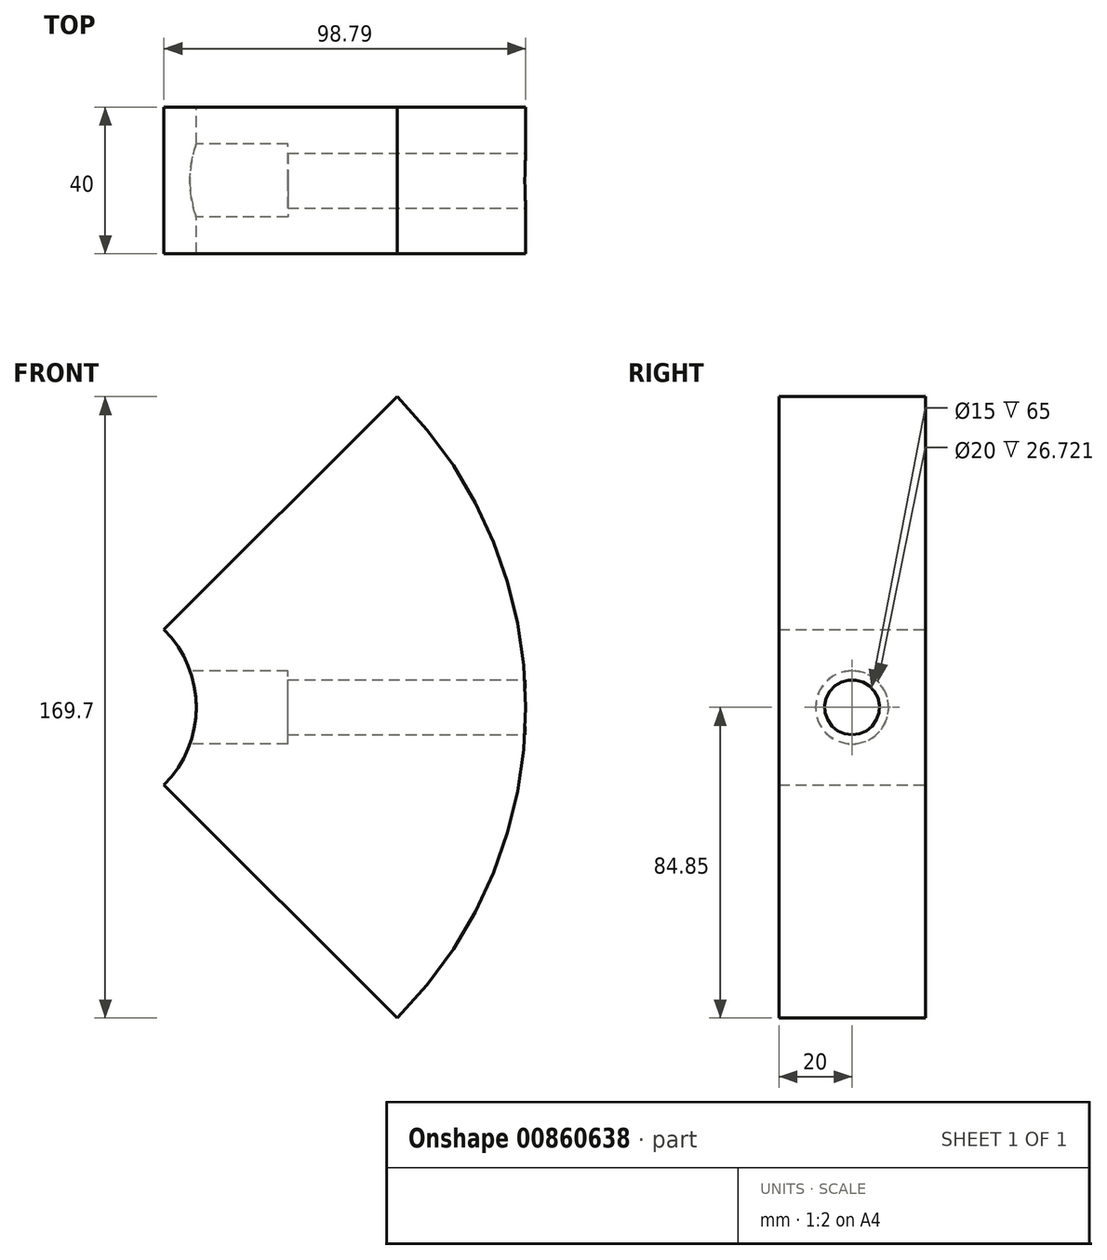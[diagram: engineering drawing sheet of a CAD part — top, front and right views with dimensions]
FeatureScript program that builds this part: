
annotation { "Feature Type Name" : "Feature", "Feature Type Description" : "" }
export const myFeature = defineFeature(function(context is Context, id is Id, definition is map)
    precondition{}
    {
        {
            var Q0;
            Q0=qCreatedBy(makeId("Front.planeOp"),FACE);
            var sketch = newSketch(context, id + "F0", { "sketchPlane" : qUnion([Q0])});
            skArc(sketch, "E0", {"start": v(84.85, -84.85) * mm, "mid": v(120, 0) * mm, "end": v(84.85, 84.85) * mm});
            skArc(sketch, "E1", {"start": v(21.21, -21.21) * mm, "mid": v(30, 0) * mm, "end": v(21.21, 21.21) * mm});
            skLineSegment(sketch, "E2", {"start": v(21.21, 21.21) * mm, "end": v(84.85, 84.85) * mm});
            skLineSegment(sketch, "E3", {"start": v(21.21, -21.21) * mm, "end": v(84.85, -84.85) * mm});
            skSolve(sketch);
        }
        {
            var Q0;
            Q0=qSketchRegion(id+"F0",true);
            extrude(context, id + "F1", {"entities" : qUnion([Q0]), "endBound" : BoundingType.SYMMETRIC, "depth" : 40 * mm, "offsetDistance" : 25 * mm});
        }
        {
            var Q0;
            Q0=qCreatedBy(makeId("Top.planeOp"),FACE);
            var sketch = newSketch(context, id + "F2", { "sketchPlane" : qUnion([Q0])});
            skCircle(sketch, "E4", {"center": v(0, 0) * mm, "radius": 7.5 * mm});
            skSolve(sketch);
        }
        {
            var Q0;
            Q0=qSketchRegion(id+"F2",true);
            extrude(context, id + "F3", {"entities" : qUnion([Q0]), "operationType" : NewBodyOperationType.REMOVE, "endBound" : BoundingType.SYMMETRIC, "oppositeDirection" : true, "depth" : 245.8 * mm, "offsetDistance" : 25 * mm});
        }
        {
            var Q0;
            Q0=qCreatedBy(makeId("Top.planeOp"),FACE);
            var sketch = newSketch(context, id + "F4", { "sketchPlane" : qUnion([Q0])});
            skCircle(sketch, "E5", {"center": v(0, 0) * mm, "radius": 10 * mm});
            skSolve(sketch);
        }
        {
            var Q0;
            Q0=qSketchRegion(id+"F4",true);
            extrude(context, id + "F5", {"entities" : qUnion([Q0]), "operationType" : NewBodyOperationType.REMOVE, "endBound" : BoundingType.SYMMETRIC, "depth" : 110 * mm, "offsetDistance" : 25 * mm});
        }
        {
            var Q0;
            Q0=qCreatedBy(makeId("Right.planeOp"),FACE);
            var sketch = newSketch(context, id + "F6", { "sketchPlane" : qUnion([Q0])});
            skCircle(sketch, "E6", {"center": v(0, 0) * mm, "radius": 7.5 * mm});
            skSolve(sketch);
        }
        {
            var Q0;
            Q0=qSketchRegion(id+"F6",true);
            extrude(context, id + "F7", {"entities" : qUnion([Q0]), "operationType" : NewBodyOperationType.REMOVE, "endBound" : BoundingType.SYMMETRIC, "oppositeDirection" : true, "depth" : 250 * mm, "offsetDistance" : 25 * mm});
        }
        {
            var Q0;
            Q0=qCreatedBy(makeId("Right.planeOp"),FACE);
            var sketch = newSketch(context, id + "F8", { "sketchPlane" : qUnion([Q0])});
            skCircle(sketch, "E7", {"center": v(0, 0) * mm, "radius": 10 * mm});
            skSolve(sketch);
        }
        {
            var Q0;
            Q0=qSketchRegion(id+"F8",true);
            extrude(context, id + "F9", {"entities" : qUnion([Q0]), "operationType" : NewBodyOperationType.REMOVE, "endBound" : BoundingType.SYMMETRIC, "depth" : 110 * mm, "offsetDistance" : 25 * mm});
        }
    });
